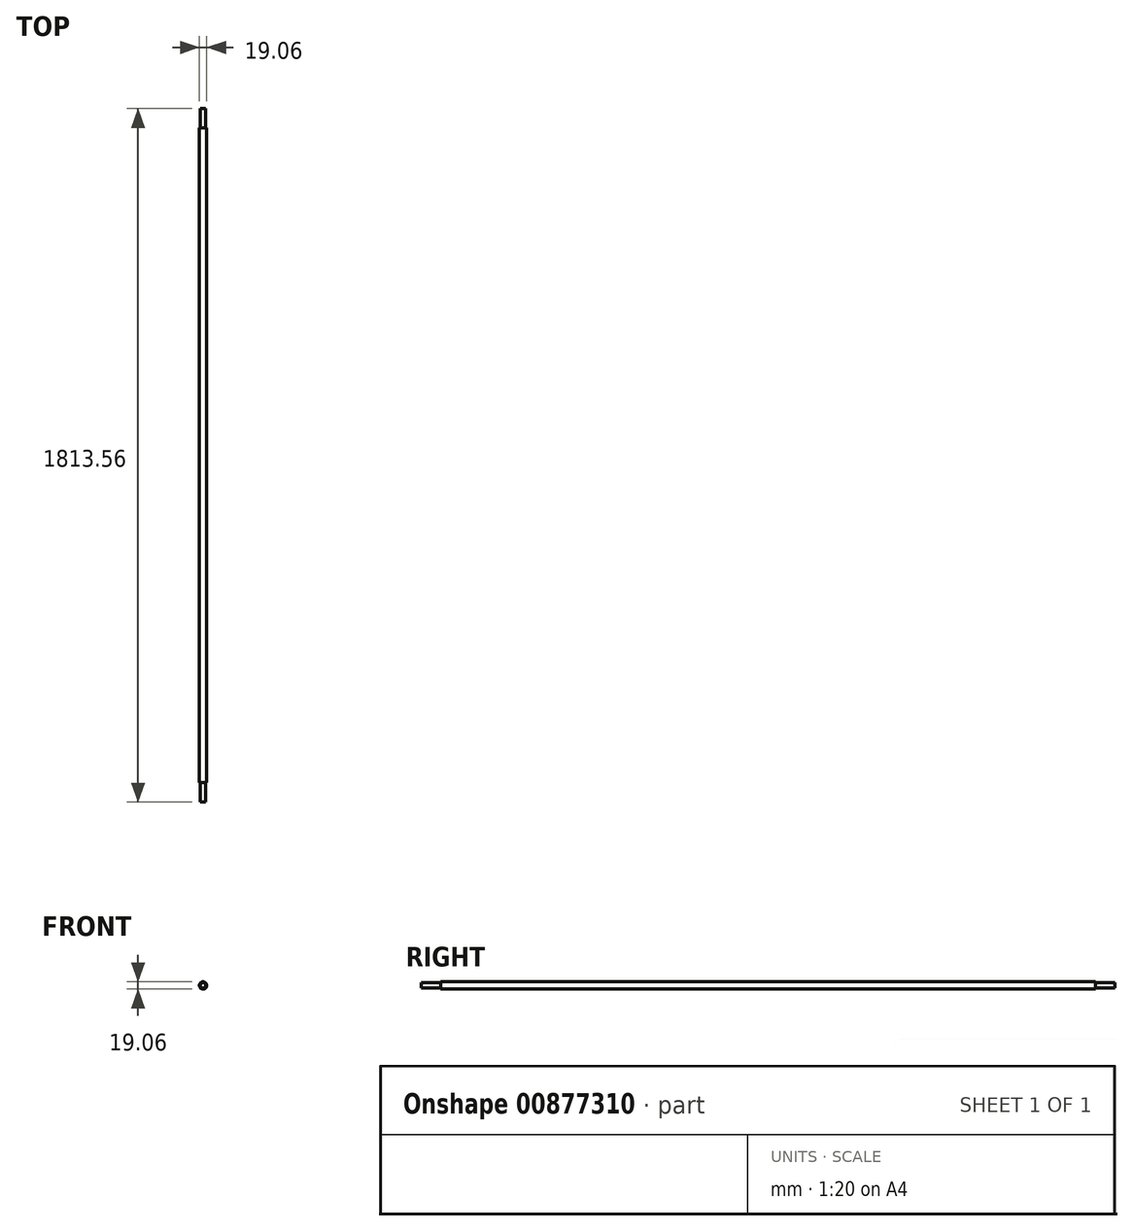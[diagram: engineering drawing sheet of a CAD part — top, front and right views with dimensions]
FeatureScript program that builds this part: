
annotation { "Feature Type Name" : "Feature", "Feature Type Description" : "" }
export const myFeature = defineFeature(function(context is Context, id is Id, definition is map)
    precondition{}
    {
        {
            var Q0;
            Q0=qCreatedBy(makeId("Front.planeOp"),FACE);
            var sketch = newSketch(context, id + "F0", { "sketchPlane" : qUnion([Q0])});
            skCircle(sketch, "E0", {"center": v(0, 0) * mm, "radius": 7.14 * mm});
            skCircle(sketch, "E1", {"center": v(0, 0) * mm, "radius": 9.53 * mm});
            skSolve(sketch);
        }
        {
            var Q0;
            Q0=makeQuery(id+"F0.imprint","IMPRINT",FACE,{"disambiguationData":[TD([[makeQuery(id+"F0.imprint","IMPRINT",EDGE,{"derivedFrom":sQuery(id+"F0.wireOp",EDGE,"E0")}),-1.0]])]});
            var Q1;
            Q1=qSketchRegion(id+"F2",true);
            extrude(context, id + "F1", {"entities" : qUnion([Q0, Q1]), "depth" : 855.98 * mm, "offsetDistance" : 25.4 * mm, "hasSecondDirection" : true, "secondDirectionOppositeDirection" : true, "secondDirectionDepth" : 855.98 * mm});
        }
        {
            var Q0;
            Q0=qCreatedBy(makeId("Front.planeOp"),FACE);
            var sketch = newSketch(context, id + "F2", { "sketchPlane" : qUnion([Q0])});
            skCircle(sketch, "E2", {"center": v(0, 0) * mm, "radius": 7.14 * mm});
            skSolve(sketch);
        }
        {
            var Q0;
            Q0=makeQuery(id+"F2.imprint","IMPRINT",FACE,{"disambiguationData":[TD([[makeQuery(id+"F2.imprint","IMPRINT",EDGE,{"derivedFrom":sQuery(id+"F2.wireOp",EDGE,"E2")}),1.0]])]});
            extrude(context, id + "F3", {"entities" : qUnion([Q0]), "operationType" : NewBodyOperationType.ADD, "depth" : 906.78 * mm, "offsetDistance" : 25.4 * mm, "hasSecondDirection" : true, "secondDirectionOppositeDirection" : true, "secondDirectionDepth" : 906.78 * mm});
        }
    });
